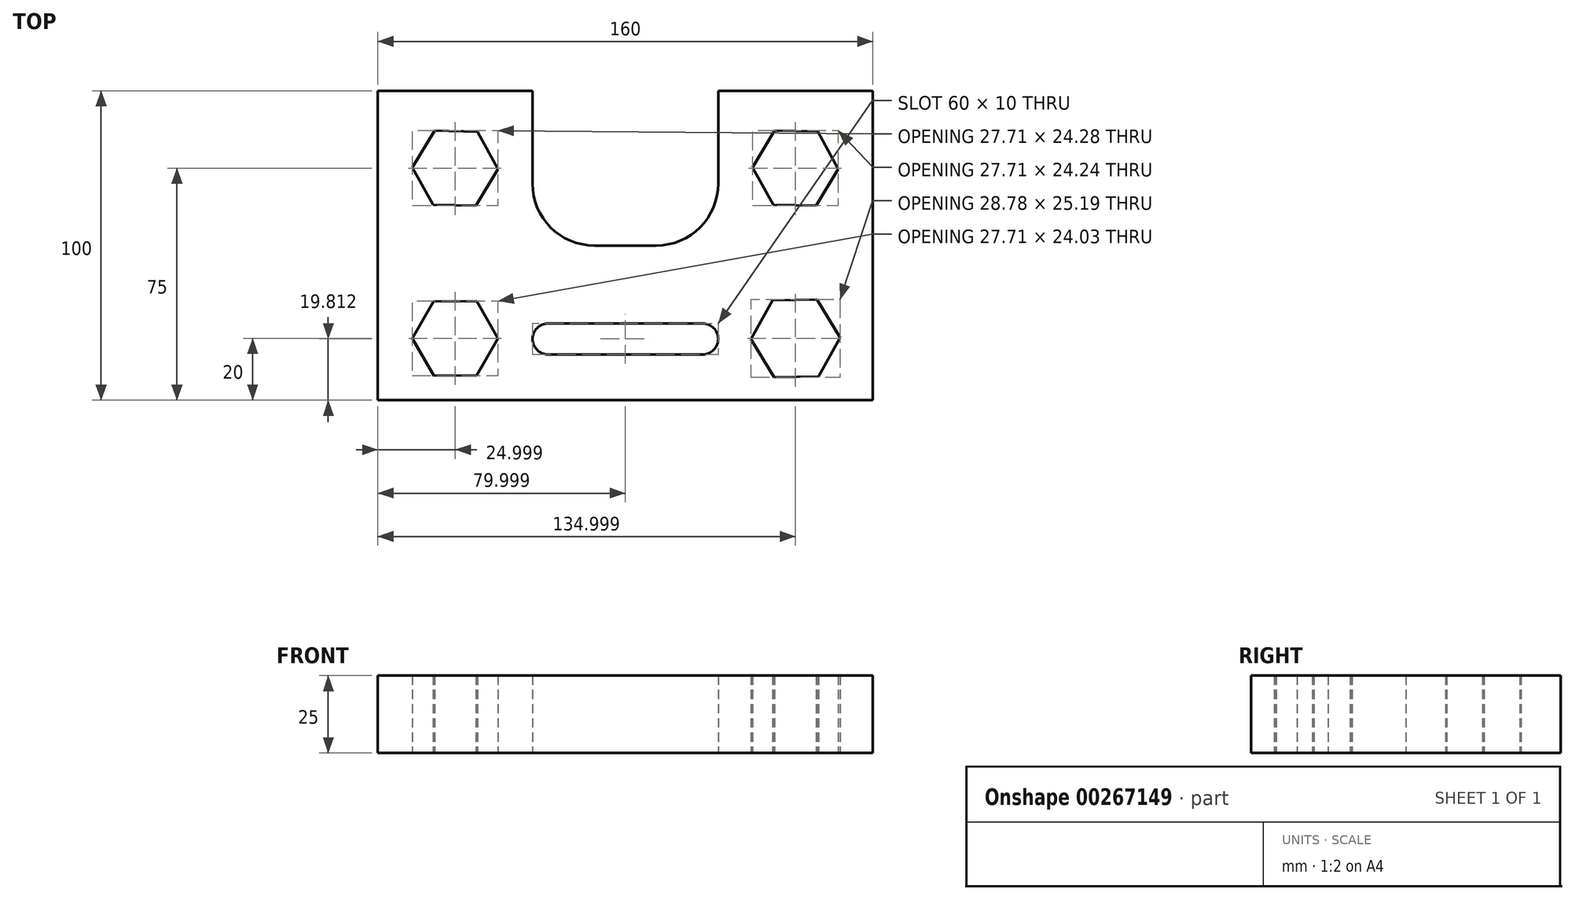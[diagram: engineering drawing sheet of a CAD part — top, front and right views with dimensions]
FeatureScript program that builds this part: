
annotation { "Feature Type Name" : "Feature", "Feature Type Description" : "" }
export const myFeature = defineFeature(function(context is Context, id is Id, definition is map)
    precondition{}
    {
        {
            var Q0;
            Q0=qCreatedBy(makeId("Top.planeOp"),FACE);
            var sketch = newSketch(context, id + "F0", { "sketchPlane" : qUnion([Q0])});
            skLineSegment(sketch, "E0.bottom", {"start": v(-81.41, 67.58) * mm, "end": v(-31.41, 67.58) * mm});
            skLineSegment(sketch, "E0.top", {"start": v(-81.41, -32.42) * mm, "end": v(78.59, -32.42) * mm});
            skLineSegment(sketch, "E0.left", {"start": v(-81.41, 67.58) * mm, "end": v(-81.41, -32.42) * mm});
            skLineSegment(sketch, "E0.right", {"start": v(78.59, 67.58) * mm, "end": v(78.59, -32.42) * mm});
            skLineSegment(sketch, "E1.top", {"start": v(-11.41, 17.58) * mm, "end": v(8.59, 17.58) * mm});
            skLineSegment(sketch, "E1.left", {"start": v(-31.41, 67.58) * mm, "end": v(-31.41, 37.58) * mm});
            skLineSegment(sketch, "E1.right", {"start": v(28.59, 67.58) * mm, "end": v(28.59, 37.58) * mm});
            skLineSegment(sketch, "E2.trimOffspring", {"start": v(28.59, 67.58) * mm, "end": v(78.59, 67.58) * mm});
            skPoint(sketch, "E3.visualSharp", {"position": v(-31.41, 17.58) * mm});
            skArc(sketch, "E3.filletArc", {"start": v(-31.41, 37.58) * mm, "mid": v(-25.55, 23.44) * mm, "end": v(-11.41, 17.58) * mm});
            skPoint(sketch, "E4.visualSharp", {"position": v(28.59, 17.58) * mm});
            skArc(sketch, "E4.filletArc", {"start": v(8.59, 17.58) * mm, "mid": v(22.73, 23.44) * mm, "end": v(28.59, 37.58) * mm});
            skLineSegment(sketch, "E5", {"start": v(53.59, -24.88) * mm, "end": v(53.59, -27.2) * mm});
            skLineSegment(sketch, "E6", {"start": v(53.59, -32.42) * mm, "end": v(78.59, -32.42) * mm});
            skLineSegment(sketch, "E7.top", {"start": v(65.59, 42.58) * mm, "end": v(67.3, 42.58) * mm});
            skLineSegment(sketch, "E7.left", {"start": v(53.59, -27.2) * mm, "end": v(53.59, -24.88) * mm});
            skCircle(sketch, "E8", {"center": v(53.59, 42.58) * mm, "radius": 12 * mm});
            skCircle(sketch, "E9", {"center": v(53.59, -12.42) * mm, "radius": 12.46 * mm});
            skLineSegment(sketch, "E10.bottom", {"start": v(-81.41, -32.42) * mm, "end": v(-56.41, -32.42) * mm});
            skLineSegment(sketch, "E10.top", {"start": v(-70.25, -12.42) * mm, "end": v(-68.41, -12.42) * mm});
            skLineSegment(sketch, "E10.left", {"start": v(-81.41, -32.42) * mm, "end": v(-81.41, -12.42) * mm});
            skLineSegment(sketch, "E11.top", {"start": v(-70.1, 42.58) * mm, "end": v(-68.41, 42.58) * mm});
            skLineSegment(sketch, "E11.left", {"start": v(-81.41, -32.42) * mm, "end": v(-81.41, 42.58) * mm});
            skCircle(sketch, "E12", {"center": v(-56.41, 42.58) * mm, "radius": 12 * mm});
            skCircle(sketch, "E13", {"center": v(-56.41, -12.42) * mm, "radius": 12 * mm});
            skCircle(sketch, "E14.cCircle", {"center": v(-56.41, -12.42) * mm, "radius": 12 * mm, "construction": true});
            skLineSegment(sketch, "E14.0", {"start": v(-49.51, -0.4) * mm, "end": v(-42.55, -12.39) * mm});
            skLineSegment(sketch, "E14.1", {"start": v(-42.55, -12.39) * mm, "end": v(-49.46, -24.4) * mm});
            skLineSegment(sketch, "E14.2", {"start": v(-49.46, -24.4) * mm, "end": v(-63.31, -24.44) * mm});
            skLineSegment(sketch, "E14.3", {"start": v(-63.31, -24.44) * mm, "end": v(-70.27, -12.45) * mm});
            skLineSegment(sketch, "E14.4", {"start": v(-70.27, -12.45) * mm, "end": v(-63.37, -0.44) * mm});
            skLineSegment(sketch, "E14.5", {"start": v(-63.37, -0.44) * mm, "end": v(-49.51, -0.4) * mm});
            skPoint(sketch, "E14.0.midPoint", {"position": v(-46.03, -6.4) * mm});
            skCircle(sketch, "E15.cCircle", {"center": v(53.59, -12.42) * mm, "radius": 12.46 * mm, "construction": true});
            skLineSegment(sketch, "E15.0", {"start": v(60.55, 0.17) * mm, "end": v(67.98, -12.15) * mm});
            skLineSegment(sketch, "E15.1", {"start": v(67.98, -12.15) * mm, "end": v(61.01, -24.75) * mm});
            skLineSegment(sketch, "E15.2", {"start": v(61.01, -24.75) * mm, "end": v(46.62, -25.01) * mm});
            skLineSegment(sketch, "E15.3", {"start": v(46.62, -25.01) * mm, "end": v(39.2, -12.69) * mm});
            skLineSegment(sketch, "E15.4", {"start": v(39.2, -12.69) * mm, "end": v(46.16, -0.1) * mm});
            skLineSegment(sketch, "E15.5", {"start": v(46.16, -0.1) * mm, "end": v(60.55, 0.17) * mm});
            skPoint(sketch, "E15.0.midPoint", {"position": v(64.27, -6) * mm});
            skCircle(sketch, "E16.cCircle", {"center": v(53.59, 42.58) * mm, "radius": 12 * mm, "construction": true});
            skLineSegment(sketch, "E16.0", {"start": v(60.72, 54.46) * mm, "end": v(67.44, 42.34) * mm});
            skLineSegment(sketch, "E16.1", {"start": v(67.44, 42.34) * mm, "end": v(60.3, 30.46) * mm});
            skLineSegment(sketch, "E16.2", {"start": v(60.3, 30.46) * mm, "end": v(46.45, 30.7) * mm});
            skLineSegment(sketch, "E16.3", {"start": v(46.45, 30.7) * mm, "end": v(39.73, 42.82) * mm});
            skLineSegment(sketch, "E16.4", {"start": v(39.73, 42.82) * mm, "end": v(46.87, 54.7) * mm});
            skLineSegment(sketch, "E16.5", {"start": v(46.87, 54.7) * mm, "end": v(60.72, 54.46) * mm});
            skPoint(sketch, "E16.0.midPoint", {"position": v(64.08, 48.4) * mm});
            skCircle(sketch, "E17.cCircle", {"center": v(-56.41, 42.58) * mm, "radius": 12 * mm, "construction": true});
            skLineSegment(sketch, "E17.0", {"start": v(-49.24, 54.43) * mm, "end": v(-42.56, 42.3) * mm});
            skLineSegment(sketch, "E17.1", {"start": v(-42.56, 42.3) * mm, "end": v(-49.73, 30.44) * mm});
            skLineSegment(sketch, "E17.2", {"start": v(-49.73, 30.44) * mm, "end": v(-63.59, 30.73) * mm});
            skLineSegment(sketch, "E17.3", {"start": v(-63.59, 30.73) * mm, "end": v(-70.26, 42.87) * mm});
            skLineSegment(sketch, "E17.4", {"start": v(-70.26, 42.87) * mm, "end": v(-63.09, 54.72) * mm});
            skLineSegment(sketch, "E17.5", {"start": v(-63.09, 54.72) * mm, "end": v(-49.24, 54.43) * mm});
            skPoint(sketch, "E17.0.midPoint", {"position": v(-45.9, 48.36) * mm});
            skLineSegment(sketch, "E18.trimOffspring", {"start": v(-56.41, 30.58) * mm, "end": v(-56.41, 30.58) * mm});
            skLineSegment(sketch, "E19.trimOffspring", {"start": v(78.59, 42.58) * mm, "end": v(82.6, 42.58) * mm});
            skLineSegment(sketch, "E20.trimOffspring", {"start": v(67.83, -12.42) * mm, "end": v(66.05, -12.42) * mm});
            skLineSegment(sketch, "E21.trimOffspring", {"start": v(53.59, 0.04) * mm, "end": v(53.59, 0.05) * mm});
            skLineSegment(sketch, "E22.trimOffspring", {"start": v(53.59, 30.58) * mm, "end": v(53.59, 30.58) * mm});
            skPoint(sketch, "E23.start.orphan", {"position": v(82.42, -32.42) * mm});
            skLineSegment(sketch, "E24.trimOffspring", {"start": v(82.42, -32.42) * mm, "end": v(82.6, -32.42) * mm});
            skLineSegment(sketch, "E25", {"start": v(-31.41, -32.42) * mm, "end": v(28.59, -32.42) * mm});
            skLineSegment(sketch, "E26.trimOffspring", {"start": v(28.59, 37.58) * mm, "end": v(28.59, 67.58) * mm});
            skPoint(sketch, "E27.oppositeSnap0", {"position": v(-66.82, -6.44) * mm});
            skLineSegment(sketch, "E27.bottom", {"start": v(-81.41, -32.42) * mm, "end": v(-26.41, -32.42) * mm});
            skLineSegment(sketch, "E27.left", {"start": v(-81.41, -32.42) * mm, "end": v(-81.41, -6.44) * mm});
            skLineSegment(sketch, "E27.right", {"start": v(-26.41, -7.6) * mm, "end": v(-26.41, -6.44) * mm});
            skLineSegment(sketch, "E28.bottom", {"start": v(-26.41, -7.6) * mm, "end": v(23.59, -7.6) * mm});
            skLineSegment(sketch, "E28.top", {"start": v(-26.41, -17.6) * mm, "end": v(23.59, -17.6) * mm});
            skArc(sketch, "E29", {"start": v(23.59, -17.6) * mm, "mid": v(28.59, -12.6) * mm, "end": v(23.59, -7.6) * mm});
            skArc(sketch, "E30", {"start": v(-26.41, -7.6) * mm, "mid": v(-31.41, -12.6) * mm, "end": v(-26.41, -17.6) * mm});
            skSolve(sketch);
        }
        {
            var Q0;
            Q0 = qSketchRegion(id + "F0", true);
            extrude(context, id + "F1", {"entities" : qUnion([Q0]), "depth" : 25 * mm});
        }
    });
